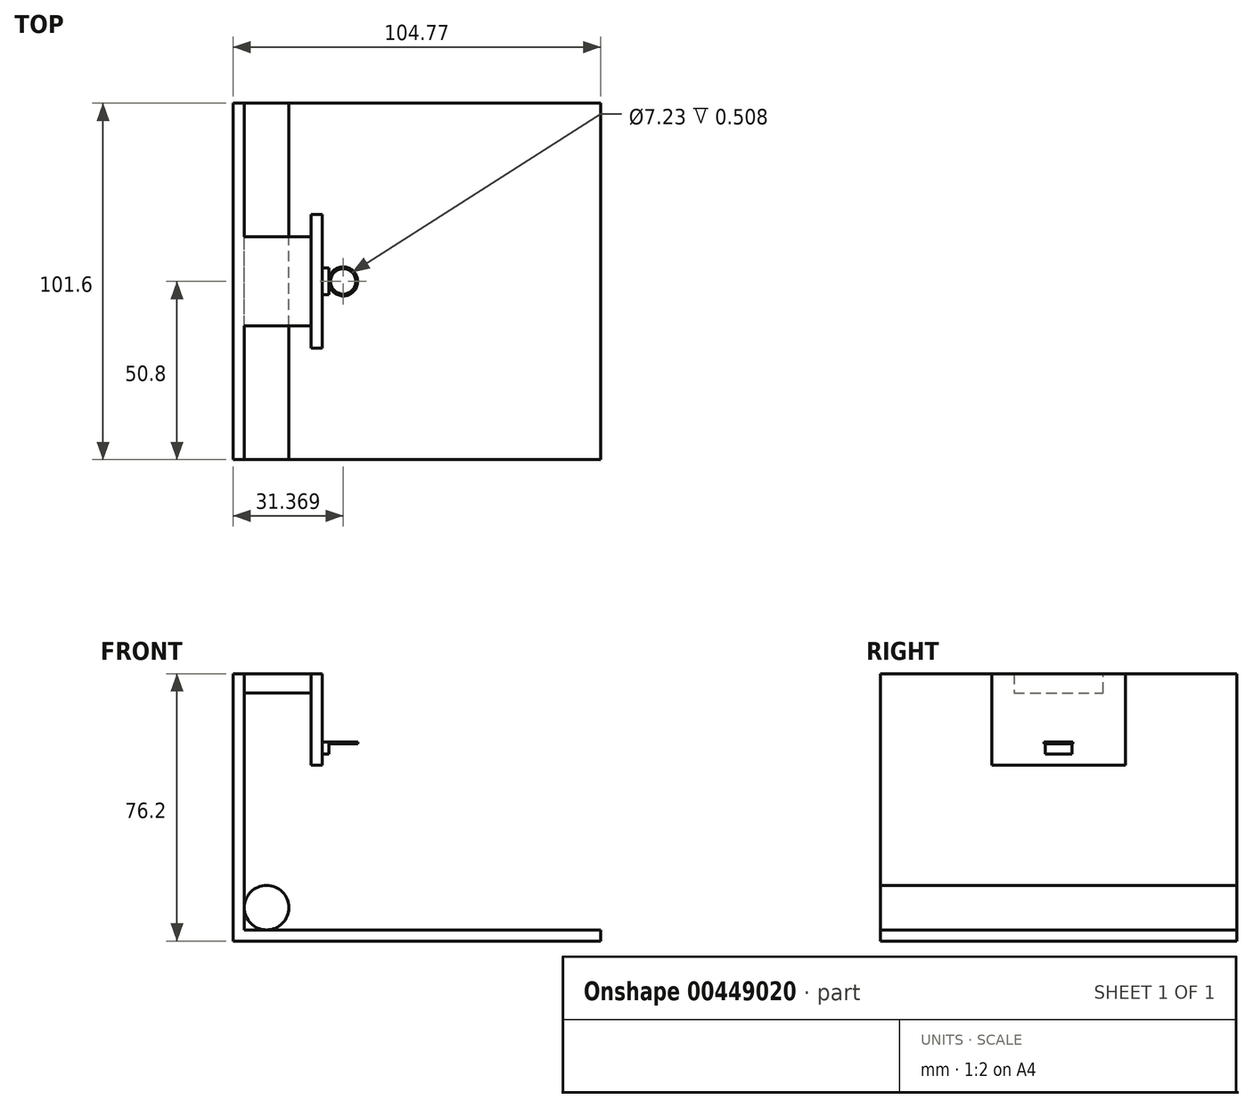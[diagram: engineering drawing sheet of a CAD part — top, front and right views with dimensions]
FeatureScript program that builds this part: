
annotation { "Feature Type Name" : "Feature", "Feature Type Description" : "" }
export const myFeature = defineFeature(function(context is Context, id is Id, definition is map)
    precondition{}
    {
        {
            var Q0;
            Q0=qCreatedBy(makeId("Front.planeOp"),FACE);
            var sketch = newSketch(context, id + "F0", { "sketchPlane" : qUnion([Q0])});
            skLineSegment(sketch, "E0", {"start": v(0, 0) * mm, "end": v(104.78, 0) * mm});
            skLineSegment(sketch, "E1", {"start": v(104.78, 0) * mm, "end": v(104.78, 3.18) * mm});
            skLineSegment(sketch, "E2", {"start": v(104.78, 3.18) * mm, "end": v(3.18, 3.17) * mm});
            skLineSegment(sketch, "E3", {"start": v(3.18, 3.17) * mm, "end": v(3.18, 76.2) * mm});
            skLineSegment(sketch, "E4", {"start": v(3.18, 76.2) * mm, "end": v(0, 76.2) * mm});
            skLineSegment(sketch, "E5", {"start": v(0, 76.2) * mm, "end": v(0, 0) * mm});
            skCircle(sketch, "E6", {"center": v(9.53, 9.52) * mm, "radius": 6.35 * mm});
            skSolve(sketch);
        }
        {
            var Q0;
            Q0=makeQuery(id+"F0.imprint","IMPRINT",FACE,{"disambiguationData":[TD([[makeQuery(id+"F0.imprint","IMPRINT",EDGE,{"derivedFrom":sQuery(id+"F0.wireOp",EDGE,"E0")}),1.0]])]});
            var Q1;
            {var subQ0=sQuery(id+"F0.wireOp",EDGE,"E6");var subQ1=makeQuery(id+"F0.imprint","INTERSECT",VERTEX,{"derivedFrom":[sQuery(id+"F0.wireOp",EDGE,"E2"),subQ0]});Q1=makeQuery(id+"F0.imprint","IMPRINT",FACE,{"disambiguationData":[TD([[makeQuery(id+"F0.imprint","IMPRINT",EDGE,{"disambiguationData":[TD([[subQ1,1.0]])],"derivedFrom":subQ0}),1.0]])]});}
            extrude(context, id + "F1", {"entities" : qUnion([Q0, Q1]), "depth" : 101.6 * mm});
        }
        {
            var Q0;
            Q0=makeQuery(id+"F1.opExtrude","SWEPT_FACE",FACE,{"disambiguationData":[OSD([sQuery(id+"F0.wireOp",EDGE,"E3")])]});
            var sketch = newSketch(context, id + "F2", { "sketchPlane" : qUnion([Q0])});
            skLineSegment(sketch, "E7", {"start": v(-63.5, 76.2) * mm, "end": v(-63.5, 70.72) * mm});
            skLineSegment(sketch, "E8", {"start": v(-63.5, 70.72) * mm, "end": v(-38.1, 70.72) * mm});
            skLineSegment(sketch, "E9", {"start": v(-38.1, 70.72) * mm, "end": v(-38.1, 76.2) * mm});
            skLineSegment(sketch, "E10", {"start": v(-38.1, 76.2) * mm, "end": v(-63.5, 76.2) * mm});
            skSolve(sketch);
        }
        {
            var Q0;
            Q0=makeQuery(id+"F2.imprint","IMPRINT",FACE,{"disambiguationData":[TD([[makeQuery(id+"F2.imprint","IMPRINT",EDGE,{"derivedFrom":sQuery(id+"F2.wireOp",EDGE,"E7")}),1.0]])]});
            extrude(context, id + "F3", {"entities" : qUnion([Q0]), "operationType" : NewBodyOperationType.ADD, "depth" : 19.05 * mm});
        }
        {
            var Q0;
            Q0=makeQuery(id+"F3.opExtrude","CAP_FACE",FACE,{"disambiguationData":[OSD([sQuery(id+"F2.wireOp",EDGE,"E7"),sQuery(id+"F2.wireOp",EDGE,"E8"),sQuery(id+"F2.wireOp",EDGE,"E9"),sQuery(id+"F2.wireOp",EDGE,"E10")])],"isStart":false});
            var sketch = newSketch(context, id + "F4", { "sketchPlane" : qUnion([Q0])});
            skLineSegment(sketch, "E11", {"start": v(-38.1, 76.2) * mm, "end": v(-31.75, 76.2) * mm});
            skLineSegment(sketch, "E12", {"start": v(-31.75, 76.2) * mm, "end": v(-31.75, 50.05) * mm});
            skLineSegment(sketch, "E13", {"start": v(-31.75, 50.05) * mm, "end": v(-69.85, 50.05) * mm});
            skLineSegment(sketch, "E14", {"start": v(-69.85, 50.05) * mm, "end": v(-69.85, 76.2) * mm});
            skLineSegment(sketch, "E15", {"start": v(-69.85, 76.2) * mm, "end": v(-31.75, 76.2) * mm});
            skSolve(sketch);
        }
        {
            var Q0;
            {var subQ3=sQuery(id+"F4.wireOp",EDGE,"E12");Q0=makeQuery(id+"F4.imprint","IMPRINT",FACE,{"disambiguationData":[TD([[makeQuery(id+"F4.imprint","IMPRINT",EDGE,{"derivedFrom":subQ3}),-1.0]])]});}
            var Q1;
            {var subQ1=makeQuery(id+"F3.opExtrude","CAP_EDGE",EDGE,{"disambiguationData":[OSD([sQuery(id+"F2.wireOp",EDGE,"E7")])],"isStart":false});Q1=makeQuery(id+"F4.imprint","IMPRINT",FACE,{"disambiguationData":[TD([[makeQuery(id+"F4.imprint","IMPRINT",EDGE,{"derivedFrom":subQ1}),1.0]])]});}
            extrude(context, id + "F5", {"entities" : qUnion([Q0, Q1]), "depth" : 3.17 * mm});
        }
        {
            var Q0;
            Q0=makeQuery(id+"F5.opExtrude","CAP_FACE",FACE,{"disambiguationData":[OSD([sQuery(id+"F4.wireOp",EDGE,"E12"),sQuery(id+"F4.wireOp",EDGE,"E13"),sQuery(id+"F4.wireOp",EDGE,"E14"),sQuery(id+"F4.wireOp",EDGE,"E15")])],"isStart":false});
            var sketch = newSketch(context, id + "F6", { "sketchPlane" : qUnion([Q0])});
            skLineSegment(sketch, "E16", {"start": v(-50.8, 53.23) * mm, "end": v(-54.61, 53.23) * mm});
            skPoint(sketch, "E16.startSnap0", {"position": v(-50.8, 50.05) * mm});
            skLineSegment(sketch, "E17", {"start": v(-54.61, 53.23) * mm, "end": v(-54.61, 56.71) * mm});
            skLineSegment(sketch, "E18", {"start": v(-54.61, 56.71) * mm, "end": v(-47, 56.71) * mm});
            skLineSegment(sketch, "E19", {"start": v(-47, 56.71) * mm, "end": v(-47, 53.23) * mm});
            skLineSegment(sketch, "E20", {"start": v(-47, 53.23) * mm, "end": v(-50.8, 53.23) * mm});
            skSolve(sketch);
        }
        {
            var Q0;
            Q0=makeQuery(id+"F6.imprint","IMPRINT",FACE,{"disambiguationData":[TD([[makeQuery(id+"F6.imprint","IMPRINT",EDGE,{"derivedFrom":sQuery(id+"F6.wireOp",EDGE,"E16")}),-1.0]])]});
            extrude(context, id + "F7", {"entities" : qUnion([Q0]), "operationType" : NewBodyOperationType.ADD, "depth" : 1.9 * mm});
        }
        {
            var Q0;
            Q0=makeQuery(id+"F7.opExtrude","SWEPT_FACE",FACE,{"disambiguationData":[OSD([sQuery(id+"F6.wireOp",EDGE,"E18")])]});
            var sketch = newSketch(context, id + "F8", { "sketchPlane" : qUnion([Q0])});
            skCircle(sketch, "E21", {"center": v(31.37, -50.8) * mm, "radius": 4.13 * mm});
            skPoint(sketch, "E21.centerSnap0", {"position": v(27.3, -50.8) * mm});
            skSolve(sketch);
        }
        {
            var Q0;
            {var subQ0=sQuery(id+"F8.wireOp",EDGE,"E21");var subQ1=makeQuery(id+"F7.opExtrude","CAP_EDGE",EDGE,{"disambiguationData":[OSD([sQuery(id+"F6.wireOp",EDGE,"E18")])],"isStart":false});var subQ2=makeQuery(id+"F8.imprint","INTERSECT",VERTEX,{"disambiguationData":[OD(0.0)],"derivedFrom":[subQ1,subQ0]});Q0=makeQuery(id+"F8.imprint","IMPRINT",FACE,{"disambiguationData":[TD([[makeQuery(id+"F8.imprint","IMPRINT",EDGE,{"disambiguationData":[TD([[subQ2,-1.0]])],"derivedFrom":subQ0}),1.0]])]});}
            extrude(context, id + "F9", {"entities" : qUnion([Q0]), "oppositeDirection" : true, "depth" : 0.5 * mm});
        }
        {
            var Q0;
            Q0=makeQuery(id+"F9.opExtrude","CAP_FACE",FACE,{"disambiguationData":[OSD([sQuery(id+"F6.wireOp",EDGE,"E18"),sQuery(id+"F8.wireOp",EDGE,"E21")])],"isStart":true});
            var sketch = newSketch(context, id + "F10", { "sketchPlane" : qUnion([Q0])});
            skCircle(sketch, "E22", {"center": v(31.37, -50.8) * mm, "radius": 3.61 * mm});
            skSolve(sketch);
        }
        {
            var Q0;
            Q0=makeQuery(id+"F10.imprint","IMPRINT",FACE,{"disambiguationData":[TD([[makeQuery(id+"F10.imprint","IMPRINT",EDGE,{"derivedFrom":sQuery(id+"F10.wireOp",EDGE,"E22")}),1.0]])]});
            extrude(context, id + "F11", {"entities" : qUnion([Q0]), "operationType" : NewBodyOperationType.REMOVE, "oppositeDirection" : true, "depth" : 0.5 * mm});
        }
    });
